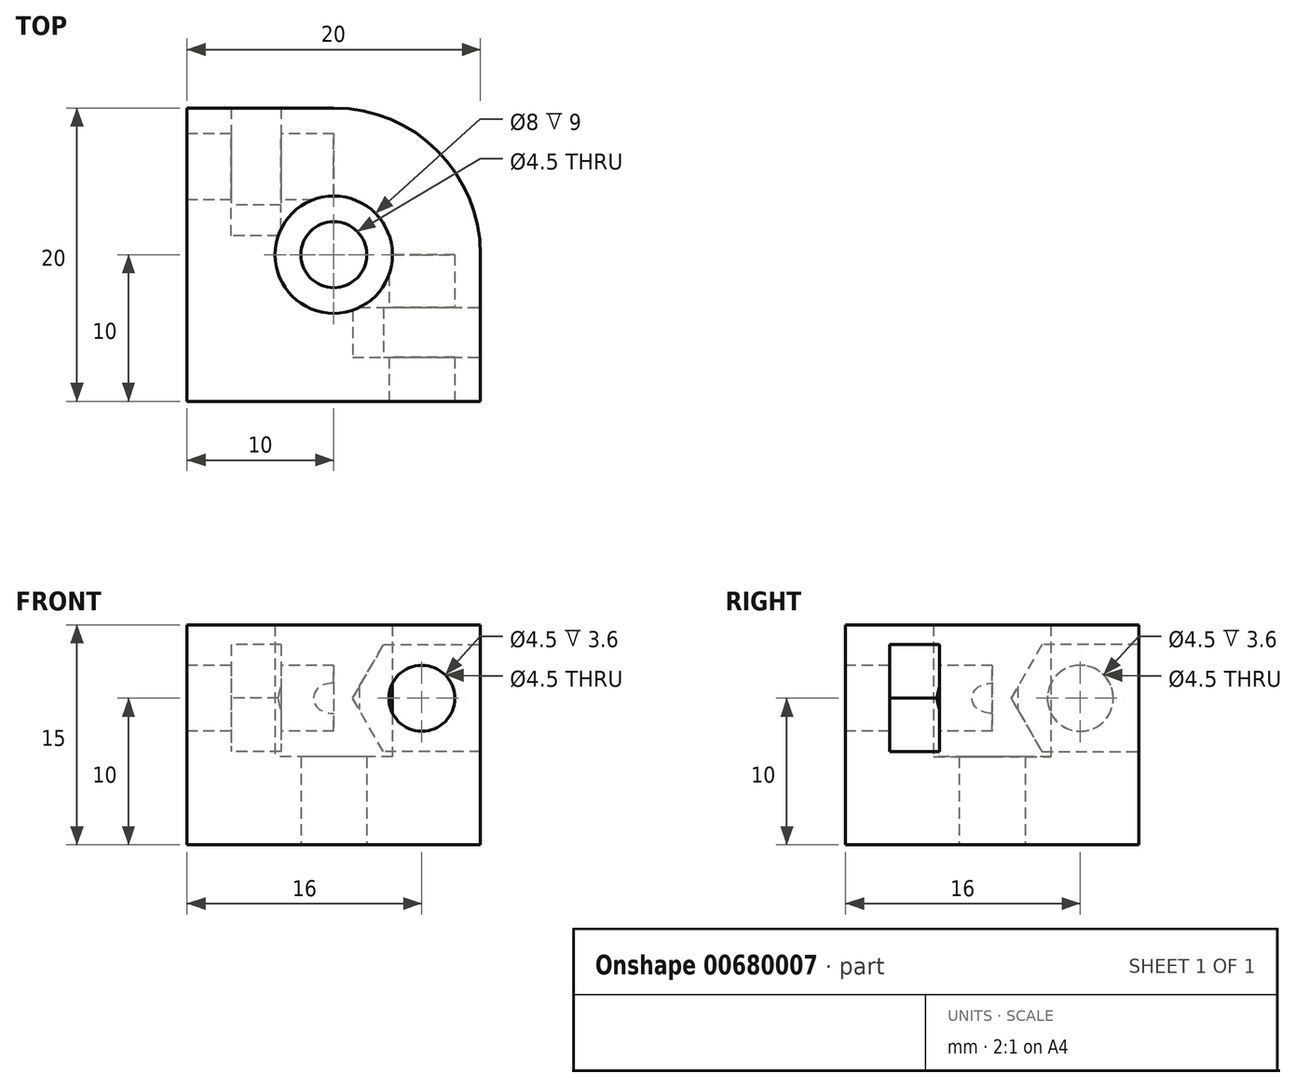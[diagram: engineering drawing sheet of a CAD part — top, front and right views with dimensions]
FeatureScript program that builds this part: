
annotation { "Feature Type Name" : "Feature", "Feature Type Description" : "" }
export const myFeature = defineFeature(function(context is Context, id is Id, definition is map)
    precondition{}
    {
        {
            var Q0;
            Q0=qCreatedBy(makeId("Top.planeOp"),FACE);
            var sketch = newSketch(context, id + "F0", { "sketchPlane" : qUnion([Q0])});
            skLineSegment(sketch, "E0", {"start": v(0, 0) * mm, "end": v(0, 20) * mm});
            skLineSegment(sketch, "E1", {"start": v(0, 20) * mm, "end": v(20, 20) * mm});
            skLineSegment(sketch, "E2", {"start": v(20, 20) * mm, "end": v(20, 0) * mm});
            skLineSegment(sketch, "E3", {"start": v(20, 0) * mm, "end": v(0, 0) * mm});
            skCircle(sketch, "E4", {"center": v(10, 10) * mm, "radius": 2.25 * mm});
            skCircle(sketch, "E5", {"center": v(10, 10) * mm, "radius": 4 * mm});
            skSolve(sketch);
        }
        {
            var Q0;
            Q0=makeQuery(id+"F0.imprint","IMPRINT",FACE,{"disambiguationData":[TD([[makeQuery(id+"F0.imprint","IMPRINT",EDGE,{"derivedFrom":sQuery(id+"F0.wireOp",EDGE,"E0")}),-1.0]])]});
            extrude(context, id + "F1", {"entities" : qUnion([Q0]), "depth" : 15 * mm});
        }
        {
            var Q0;
            Q0=makeQuery(id+"F0.imprint","IMPRINT",FACE,{"disambiguationData":[TD([[makeQuery(id+"F0.imprint","IMPRINT",EDGE,{"derivedFrom":sQuery(id+"F0.wireOp",EDGE,"E4")}),-1.0]])]});
            extrude(context, id + "F2", {"entities" : qUnion([Q0]), "operationType" : NewBodyOperationType.ADD, "depth" : 6 * mm});
        }
        {
            var Q0;
            Q0=makeQuery(id+"F1.opExtrude","SWEPT_FACE",FACE,{"disambiguationData":[OSD([sQuery(id+"F0.wireOp",EDGE,"E0")])]});
            var sketch = newSketch(context, id + "F3", { "sketchPlane" : qUnion([Q0])});
            skCircle(sketch, "E6", {"center": v(-16, 10) * mm, "radius": 2.25 * mm});
            skLineSegment(sketch, "E7.2", {"start": v(-13.4, 13.65) * mm, "end": v(-11.29, 10) * mm});
            skLineSegment(sketch, "E7.3", {"start": v(-11.29, 10) * mm, "end": v(-13.4, 6.35) * mm});
            skLineSegment(sketch, "E8", {"start": v(-20, 13.65) * mm, "end": v(-20, 6.35) * mm});
            skLineSegment(sketch, "E9", {"start": v(-20, 13.65) * mm, "end": v(-13.4, 13.65) * mm});
            skLineSegment(sketch, "E10", {"start": v(-13.4, 6.35) * mm, "end": v(-20, 6.35) * mm});
            skLineSegment(sketch, "E11", {"start": v(-16, 10) * mm, "end": v(-15.5, 10) * mm, "construction": true});
            skLineSegment(sketch, "E12", {"start": v(-15.5, 10) * mm, "end": v(-11.29, 10) * mm, "construction": true});
            skLineSegment(sketch, "E13", {"start": v(-12.34, 11.83) * mm, "end": v(-15.5, 10) * mm, "construction": true});
            skSolve(sketch);
        }
        {
            var Q0;
            Q0=makeQuery(id+"F3.imprint","IMPRINT",FACE,{"disambiguationData":[TD([[makeQuery(id+"F3.imprint","IMPRINT",EDGE,{"derivedFrom":sQuery(id+"F3.wireOp",EDGE,"E6")}),1.0]])]});
            extrude(context, id + "F4", {"entities" : qUnion([Q0]), "operationType" : NewBodyOperationType.REMOVE, "oppositeDirection" : true, "depth" : 10 * mm});
        }
        {
            var Q0;
            Q0=qSketchRegion(id+"F3",true);
            extrude(context, id + "F5", {"entities" : qUnion([Q0]), "operationType" : NewBodyOperationType.REMOVE, "oppositeDirection" : true, "depth" : (3.4 + 3) * mm});
        }
        {
            var Q0;
            Q0=makeQuery(id+"F3.imprint","IMPRINT",FACE,{"disambiguationData":[TD([[makeQuery(id+"F3.imprint","IMPRINT",EDGE,{"derivedFrom":sQuery(id+"F3.wireOp",EDGE,"E6")}),-1.0]])]});
            extrude(context, id + "F6", {"entities" : qUnion([Q0]), "operationType" : NewBodyOperationType.ADD, "oppositeDirection" : true, "depth" : 3 * mm});
        }
        {
            var Q0;
            Q0=makeQuery(id+"F1.opExtrude","SWEPT_FACE",FACE,{"disambiguationData":[OSD([sQuery(id+"F0.wireOp",EDGE,"E3")])]});
            var sketch = newSketch(context, id + "F7", { "sketchPlane" : qUnion([Q0])});
            skCircle(sketch, "E14", {"center": v(16, 10) * mm, "radius": 2.25 * mm});
            skLineSegment(sketch, "E15.4", {"start": v(13.4, 6.35) * mm, "end": v(11.29, 10) * mm});
            skLineSegment(sketch, "E15.5", {"start": v(11.29, 10) * mm, "end": v(13.4, 13.65) * mm});
            skLineSegment(sketch, "E16", {"start": v(20, 13.65) * mm, "end": v(20, 6.35) * mm});
            skLineSegment(sketch, "E17", {"start": v(11.29, 10) * mm, "end": v(15.5, 10) * mm, "construction": true});
            skLineSegment(sketch, "E18", {"start": v(15.5, 10) * mm, "end": v(16, 10) * mm, "construction": true});
            skLineSegment(sketch, "E19", {"start": v(15.5, 10) * mm, "end": v(12.34, 11.83) * mm, "construction": true});
            skLineSegment(sketch, "E20", {"start": v(13.4, 13.65) * mm, "end": v(20, 13.65) * mm});
            skLineSegment(sketch, "E21", {"start": v(20, 6.35) * mm, "end": v(13.4, 6.35) * mm});
            skSolve(sketch);
        }
        {
            var Q0;
            Q0=makeQuery(id+"F7.imprint","IMPRINT",FACE,{"disambiguationData":[TD([[makeQuery(id+"F7.imprint","IMPRINT",EDGE,{"derivedFrom":sQuery(id+"F7.wireOp",EDGE,"E14")}),1.0]])]});
            extrude(context, id + "F8", {"entities" : qUnion([Q0]), "operationType" : NewBodyOperationType.REMOVE, "oppositeDirection" : true, "depth" : 10 * mm});
        }
        {
            var Q0;
            Q0=makeQuery(id+"F7.imprint","IMPRINT",FACE,{"disambiguationData":[TD([[makeQuery(id+"F7.imprint","IMPRINT",EDGE,{"derivedFrom":sQuery(id+"F7.wireOp",EDGE,"E14")}),-1.0]])]});
            extrude(context, id + "F9", {"entities" : qUnion([Q0]), "operationType" : NewBodyOperationType.REMOVE, "oppositeDirection" : true, "depth" : (3.4 + 3) * mm});
        }
        {
            var Q0;
            Q0=makeQuery(id+"F7.imprint","IMPRINT",FACE,{"disambiguationData":[TD([[makeQuery(id+"F7.imprint","IMPRINT",EDGE,{"derivedFrom":sQuery(id+"F7.wireOp",EDGE,"E14")}),-1.0]])]});
            extrude(context, id + "F10", {"entities" : qUnion([Q0]), "operationType" : NewBodyOperationType.ADD, "oppositeDirection" : true, "depth" : 3 * mm});
        }
        {
            var Q0;
            Q0=makeQuery(id+"F1.opExtrude","SWEPT_EDGE",EDGE,{"disambiguationData":[OSD([sQuery(id+"F0.wireOp",EDGE,"E1"),sQuery(id+"F0.wireOp",EDGE,"E2")])]});
            fillet(context, id + "F11", {"entities" : qUnion([Q0]), "radius" : 10 * mm, "tangentPropagation" : true, "allowEdgeOverflow" : false});
        }
    });
